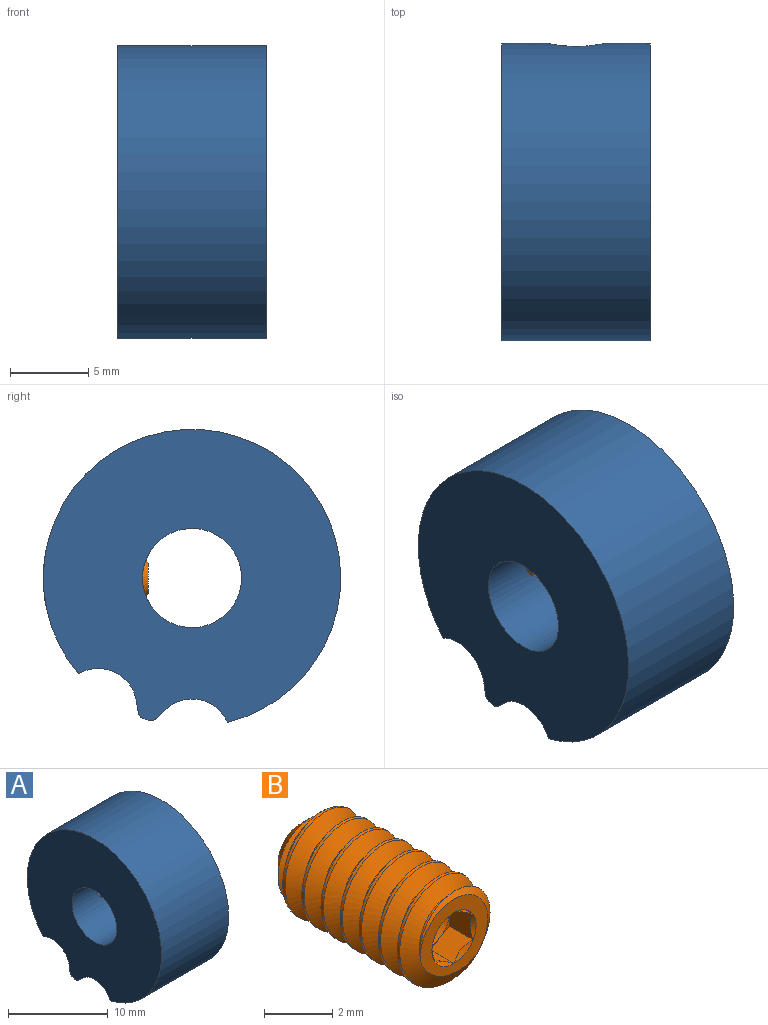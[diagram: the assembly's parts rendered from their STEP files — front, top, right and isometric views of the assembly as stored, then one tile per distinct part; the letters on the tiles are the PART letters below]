
ASSEMBLY  parts=2 mates=1
PART A: 13 faces, bbox 9.5x19.1x18.8 mm
  f0: cylinder r=9.53mm len=19.05mm, axis (-1,0,0), area 458.2mm2, adj f1,f6,f7,f8,f10
  f1: cylinder r=2.48mm len=9.53mm, axis (-1,0,0), area 46mm2, adj f0,f2,f7,f8
  f2: plane 9.53x0.52mm, normal (0,-0.71,-0.71), area 7mm2, adj f1,f7,f8,f11
  f3: cylinder r=9.53mm len=9.53mm, axis (-1,0,0), area 3.5mm2, adj f7,f8,f11,f12
  f4: plane 9.53x0.72mm, normal (0,0.99,-0.16), area 7mm2, adj f6,f7,f8,f12
  f5: cylinder r=3.17mm len=9.53mm, axis (-1,0,0), area 184.9mm2, adj f7,f8,f9
  f6: cylinder r=2.48mm len=9.53mm, axis (-1,0,0), area 46mm2, adj f0,f4,f7,f8
  f7: plane 19.05x18.77mm, normal (1,0,0), area 241.7mm2, adj f0,f1,f2,f3,f4,f5,f6,f11
  f8: plane 19.05x18.77mm, normal (-1,0,0), area 241.7mm2, adj f0,f1,f2,f3,f4,f5,f6,f11
  f9: cylinder r=1.39mm len=6.05mm, axis (0,-1,0), area 50.7mm2, adj f5,f10
  f10: bspline ~3.81x3.64mm, area 6.6mm2, adj f0,f9
  f11: cylinder r=0.5mm len=9.53mm, axis (-1,0,0), area 5.1mm2, adj f2,f3,f7,f8
  f12: cylinder r=0.5mm len=9.53mm, axis (-1,0,0), area 5.1mm2, adj f3,f4,f7,f8
PART B: 27 faces, bbox 3.9x7x3.9 mm
  f0: cone r=0.79mm half-angle=60deg, axis (0,-1,0), area 2.3mm2, adj f1,f22,f23,f24,f25,f26
  f1: plane 0.69x0.4mm, normal (0,-1,0), area 0mm2, adj f0,f2,f21
  f2: plane 1.08x1.01mm, normal (-1,0,0), area 0.8mm2, adj f1,f3,f20,f21,f22
  f3: plane 1.34x1.14mm, normal (-0.5,0,-0.87), area 0.8mm2, adj f2,f4,f19,f22,f23
  f4: plane 1.34x1.14mm, normal (0.5,0,-0.87), area 0.8mm2, adj f3,f5,f18,f23,f24
  f5: plane 1.34x1.26mm, normal (1,0,0), area 0.8mm2, adj f4,f6,f17,f24,f25
  f6: plane 1.34x1.14mm, normal (0.5,0,0.87), area 0.8mm2, adj f5,f7,f21,f25,f26
  f7: cone r=0.92mm half-angle=45deg, axis (0,-1,0), area 0mm2, adj f6,f8
  f8: plane 2.84x2.7mm, normal (0,-1,0), area 3.2mm2, adj f7,f9,f10,f14,f15,f16,f17,f18
  f9: cone r=0.92mm half-angle=45deg, axis (0,-1,0), area 0mm2, adj f8,f21
  f10: cylinder r=1.24mm len=6.07mm, axis (0,-1,0), area 5.9mm2, adj f8,f11,f14,f16
  f11: cone r=0.96mm half-angle=45deg, axis (0,-1,0), area 6mm2, adj f10,f12,f13,f14,f16
  f12: cylinder r=1.75mm len=5.31mm, axis (0,-1,0), area 7.3mm2, adj f11,f14,f15,f16
  f13: cone r=1664.28mm half-angle=59deg, axis (0,1,0), area 3.4mm2, adj f11
  f14: bspline ~6.37x3.51mm, area 40.3mm2, adj f8,f10,f11,f12,f15
  f15: cone r=1.75mm half-angle=55deg, axis (0,1,0), area 1.6mm2, adj f8,f12,f14,f16
  f16: bspline ~6.47x3.5mm, area 40.3mm2, adj f8,f10,f11,f12,f15
  f17: cone r=0.92mm half-angle=45deg, axis (0,-1,0), area 0mm2, adj f5,f8
  f18: cone r=0.92mm half-angle=45deg, axis (0,-1,0), area 0mm2, adj f4,f8
  f19: cone r=0.92mm half-angle=45deg, axis (0,-1,0), area 0mm2, adj f3,f8
  f20: cone r=0.92mm half-angle=45deg, axis (0,-1,0), area 0.1mm2, adj f2,f8
  f21: plane 1.34x1.14mm, normal (-0.5,0,0.87), area 0.8mm2, adj f1,f2,f6,f9,f26
  f22: plane 0.69x0.4mm, normal (0,-1,0), area 0mm2, adj f0,f2,f3
  f23: plane 0.79x0.23mm, normal (0,-1,0), area 0mm2, adj f0,f3,f4
  f24: plane 0.69x0.4mm, normal (0,-1,0), area 0mm2, adj f0,f4,f5
  f25: plane 0.69x0.4mm, normal (0,-1,0), area 0mm2, adj f0,f5,f6
  f26: plane 0.79x0.23mm, normal (0,-1,0), area 0mm2, adj f0,f6,f21
PLACE A t=(-25.4,0,-92.39)mm
PLACE B rot(axis=(-1,0,0),180deg) t=(0,6.28,0)mm
MATE fastened B.f13 <-> A.f9  axis (0,1,0) through (0,2.81,0)mm
